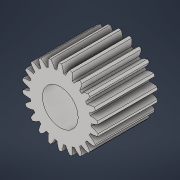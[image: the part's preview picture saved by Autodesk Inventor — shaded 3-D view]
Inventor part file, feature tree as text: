
AUTODESK INVENTOR PART (.ipt)
format: ipt  version: 2021 (Build 250183000, 183)  size: 313,856 bytes
history: native  units: mm (DEFAULTED — no unit token found)
features: plane x3, other x3, sketch x3, extrude x2
ambient origin geometry x8: Origin, YZ Plane, XZ Plane, XY Plane, X Axis, Y Axis, Z Axis, Center Point
bodies: Solid1 (feature_tree)
feature tree (11):
  extrude  "Extrusion1"  Depth=1.5mm TaperAngle=0.0deg
  plane  "Work Plane2"
  plane  "Work Plane8"
  plane  "Work Plane9"
  other  "Engrenagem reta"
  extrude  "Extrusão2"  Depth=10.0mm TaperAngle=0.0deg
  sketch  "Sketch1"  dims[d0=1.918183mm d1=1.5mm d2=0.0mm]
  sketch  "Sketch2"  dims[d3=1.76mm d4=10.0mm d5=0.0mm]
  other  "Srf1"
  sketch  "Esboço3"  dims[d16=3.188mm d17=0.0mm d34=1.427997mm d39=0.0mm d41=0.0mm d43=3.188mm d46=3.188mm d47=0.0mm d48=0.0mm d49=0.9mm d50=1.5mm d51=0.0mm]
  other  "Diâmetro do flanco"
